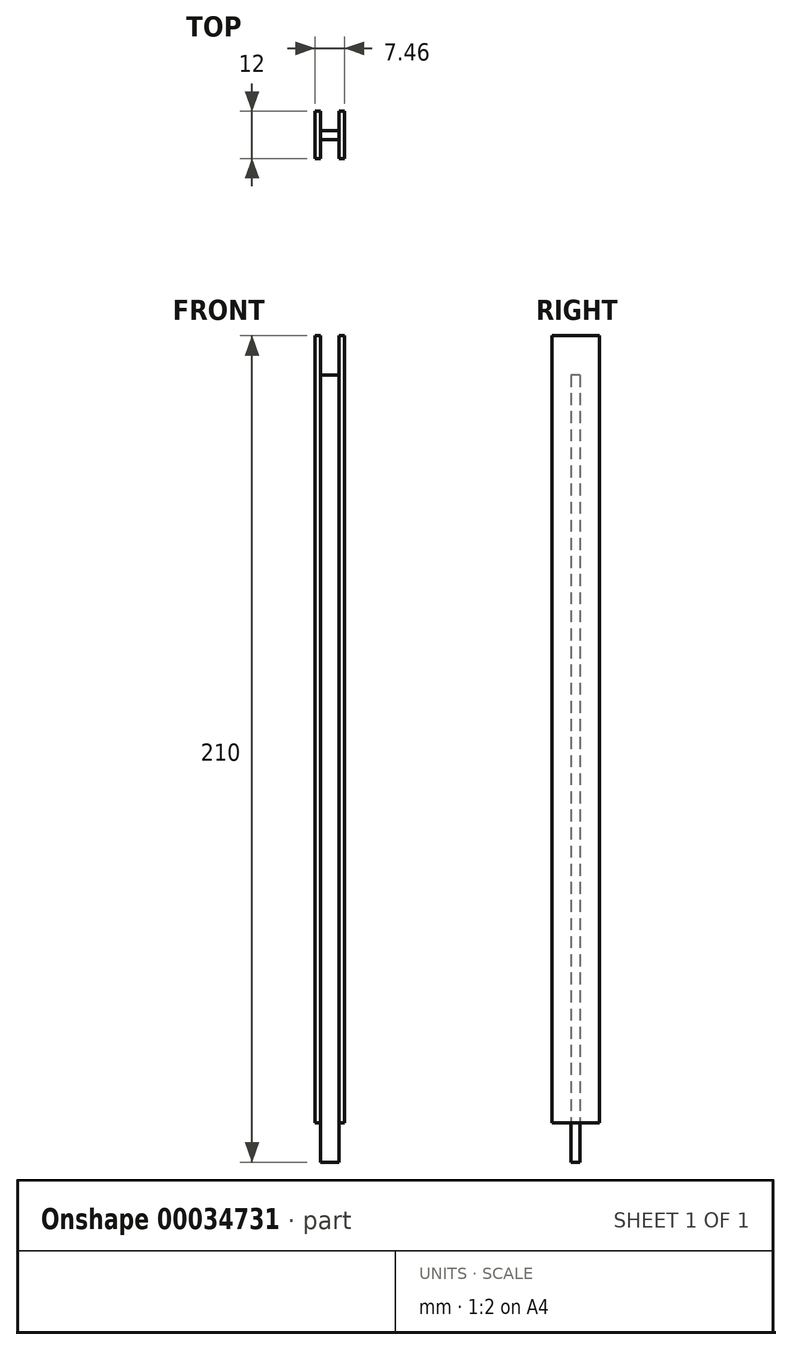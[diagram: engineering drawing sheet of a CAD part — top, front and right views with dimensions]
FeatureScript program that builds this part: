
annotation { "Feature Type Name" : "Feature", "Feature Type Description" : "" }
export const myFeature = defineFeature(function(context is Context, id is Id, definition is map)
    precondition{}
    {
        {
            var Q0;
            Q0=qCreatedBy(makeId("Top.planeOp"),FACE);
            var sketch = newSketch(context, id + "F0", { "sketchPlane" : qUnion([Q0])});
            skLineSegment(sketch, "E0", {"start": v(0, 1.14) * mm, "end": v(2.4, 1.14) * mm});
            skLineSegment(sketch, "E1", {"start": v(2.4, 1.14) * mm, "end": v(2.4, 6) * mm});
            skLineSegment(sketch, "E2", {"start": v(2.4, 6) * mm, "end": v(3.73, 6) * mm});
            skLineSegment(sketch, "E3", {"start": v(3.73, 6) * mm, "end": v(3.73, 0) * mm});
            skLineSegment(sketch, "E4.MirrorCS", {"start": v(0, 1.14) * mm, "end": v(-2.4, 1.14) * mm});
            skLineSegment(sketch, "E5.MirrorCS", {"start": v(-2.4, 6) * mm, "end": v(-3.73, 6) * mm});
            skLineSegment(sketch, "E6.MirrorCS", {"start": v(-3.73, 6) * mm, "end": v(-3.73, 0) * mm});
            skLineSegment(sketch, "E7.MirrorCS", {"start": v(-2.4, 1.14) * mm, "end": v(-2.4, 6) * mm});
            skLineSegment(sketch, "E8.MirrorCS", {"start": v(-3.73, -6) * mm, "end": v(-3.73, 0) * mm});
            skLineSegment(sketch, "E9.MirrorCS", {"start": v(-2.4, -1.14) * mm, "end": v(-2.4, -6) * mm});
            skLineSegment(sketch, "E10.MirrorCS", {"start": v(-2.4, -6) * mm, "end": v(-3.73, -6) * mm});
            skLineSegment(sketch, "E11.MirrorCS", {"start": v(0, -1.14) * mm, "end": v(-2.4, -1.14) * mm});
            skLineSegment(sketch, "E12.MirrorCS", {"start": v(0, -1.14) * mm, "end": v(2.4, -1.14) * mm});
            skLineSegment(sketch, "E13.MirrorCS", {"start": v(2.4, -1.14) * mm, "end": v(2.4, -6) * mm});
            skLineSegment(sketch, "E14.MirrorCS", {"start": v(2.4, -6) * mm, "end": v(3.73, -6) * mm});
            skLineSegment(sketch, "E15.MirrorCS", {"start": v(3.73, -6) * mm, "end": v(3.73, 0) * mm});
            skLineSegment(sketch, "E16", {"start": v(2.4, -1.14) * mm, "end": v(2.4, 1.14) * mm, "construction": true});
            skSolve(sketch);
        }
        {
            var Q0;
            Q0 = qSketchRegion(id + "F0", true);
            var Q1;
            Q1=makeQuery(id+"F0.imprint","IMPRINT",FACE,{"disambiguationData":[TD([[makeQuery(id+"F0.imprint","IMPRINT",EDGE,{"derivedFrom":sQuery(id+"F0.wireOp",EDGE,"E0")}),-1.0]])]});
            extrude(context, id + "F1", {"entities" : qUnion([Q0, Q1]), "depth" : 200 * mm, "offsetDistance" : 25 * mm});
        }
        {
            var Q0;
            Q0=makeQuery(id+"F1.opExtrude","CAP_FACE",FACE,{"disambiguationData":[OSD([sQuery(id+"F0.wireOp",EDGE,"E0"),sQuery(id+"F0.wireOp",EDGE,"E1"),sQuery(id+"F0.wireOp",EDGE,"E2"),sQuery(id+"F0.wireOp",EDGE,"E3"),sQuery(id+"F0.wireOp",EDGE,"E4.MirrorCS"),sQuery(id+"F0.wireOp",EDGE,"E5.MirrorCS"),sQuery(id+"F0.wireOp",EDGE,"E6.MirrorCS"),sQuery(id+"F0.wireOp",EDGE,"E7.MirrorCS"),sQuery(id+"F0.wireOp",EDGE,"E8.MirrorCS"),sQuery(id+"F0.wireOp",EDGE,"E9.MirrorCS"),sQuery(id+"F0.wireOp",EDGE,"E10.MirrorCS"),sQuery(id+"F0.wireOp",EDGE,"E11.MirrorCS"),sQuery(id+"F0.wireOp",EDGE,"E12.MirrorCS"),sQuery(id+"F0.wireOp",EDGE,"E13.MirrorCS"),sQuery(id+"F0.wireOp",EDGE,"E14.MirrorCS"),sQuery(id+"F0.wireOp",EDGE,"E15.MirrorCS")])],"isStart":false});
            var sketch = newSketch(context, id + "F2", { "sketchPlane" : qUnion([Q0])});
            skLineSegment(sketch, "E17", {"start": v(-2.4, -1.14) * mm, "end": v(-2.4, 1.14) * mm});
            skLineSegment(sketch, "E18", {"start": v(2.4, -1.14) * mm, "end": v(2.4, 1.14) * mm});
            skSolve(sketch);
        }
        {
            var Q0;
            Q0=makeQuery(id+"F2.imprint","IMPRINT",FACE,{"disambiguationData":[TD([[makeQuery(id+"F2.imprint","IMPRINT",EDGE,{"derivedFrom":sQuery(id+"F2.wireOp",EDGE,"E17")}),1.0]])]});
            var Q1;
            Q1=makeQuery(id+"F2.imprint","IMPRINT",FACE,{"disambiguationData":[TD([[makeQuery(id+"F2.imprint","IMPRINT",EDGE,{"derivedFrom":sQuery(id+"F2.wireOp",EDGE,"E18")}),-1.0]])]});
            extrude(context, id + "F3", {"entities" : qUnion([Q0, Q1]), "operationType" : NewBodyOperationType.ADD, "depth" : 10 * mm, "offsetDistance" : 25 * mm});
        }
        {
            var Q0;
            Q0=makeQuery(id+"F1.opExtrude","CAP_FACE",FACE,{"disambiguationData":[OSD([sQuery(id+"F0.wireOp",EDGE,"E0"),sQuery(id+"F0.wireOp",EDGE,"E1"),sQuery(id+"F0.wireOp",EDGE,"E2"),sQuery(id+"F0.wireOp",EDGE,"E3"),sQuery(id+"F0.wireOp",EDGE,"E4.MirrorCS"),sQuery(id+"F0.wireOp",EDGE,"E5.MirrorCS"),sQuery(id+"F0.wireOp",EDGE,"E6.MirrorCS"),sQuery(id+"F0.wireOp",EDGE,"E7.MirrorCS"),sQuery(id+"F0.wireOp",EDGE,"E8.MirrorCS"),sQuery(id+"F0.wireOp",EDGE,"E9.MirrorCS"),sQuery(id+"F0.wireOp",EDGE,"E10.MirrorCS"),sQuery(id+"F0.wireOp",EDGE,"E11.MirrorCS"),sQuery(id+"F0.wireOp",EDGE,"E12.MirrorCS"),sQuery(id+"F0.wireOp",EDGE,"E13.MirrorCS"),sQuery(id+"F0.wireOp",EDGE,"E14.MirrorCS"),sQuery(id+"F0.wireOp",EDGE,"E15.MirrorCS")])],"isStart":true});
            var sketch = newSketch(context, id + "F4", { "sketchPlane" : qUnion([Q0])});
            skLineSegment(sketch, "E19", {"start": v(-2.4, -1.14) * mm, "end": v(-2.4, 1.14) * mm});
            skLineSegment(sketch, "E20", {"start": v(2.4, -1.14) * mm, "end": v(2.4, 1.14) * mm});
            skSolve(sketch);
        }
        {
            var Q0;
            Q0=makeQuery(id+"F4.imprint","IMPRINT",FACE,{"disambiguationData":[TD([[makeQuery(id+"F4.imprint","IMPRINT",EDGE,{"derivedFrom":sQuery(id+"F4.wireOp",EDGE,"E20")}),-1.0]])]});
            var Q1;
            Q1=makeQuery(id+"F4.imprint","IMPRINT",FACE,{"disambiguationData":[TD([[makeQuery(id+"F4.imprint","IMPRINT",EDGE,{"derivedFrom":sQuery(id+"F4.wireOp",EDGE,"E19")}),1.0]])]});
            extrude(context, id + "F5", {"entities" : qUnion([Q0, Q1]), "operationType" : NewBodyOperationType.REMOVE, "oppositeDirection" : true, "depth" : 10 * mm, "offsetDistance" : 25 * mm});
        }
    });
